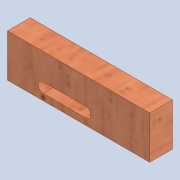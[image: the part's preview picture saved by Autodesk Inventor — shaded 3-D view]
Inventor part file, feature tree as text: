
AUTODESK INVENTOR PART (.ipt)
format: ipt  version: 2020 (Build 240168000, 168)  size: 254,976 bytes
history: native  units: mm
features: extrude x2, sketch x2
ambient origin geometry x8: Origin, YZ Plane, XZ Plane, XY Plane, X Axis, Y Axis, Z Axis, Center Point
bodies: Solid1 (feature_tree)
feature tree (4):
  extrude  "Extrusion1"  Depth=25.0mm
  extrude  "Extrusion5"  Depth=3.5mm
  sketch  "Sketch1"  dims[d0=50.0mm d1=25.0mm]
  sketch  "Sketch5"  dims[d2=8.0mm d3=0.0mm d29=3.5mm d30=4.0mm d31=4.0mm d32=20.0mm d33=15.0mm d34=15.0mm d35=0.0mm]
